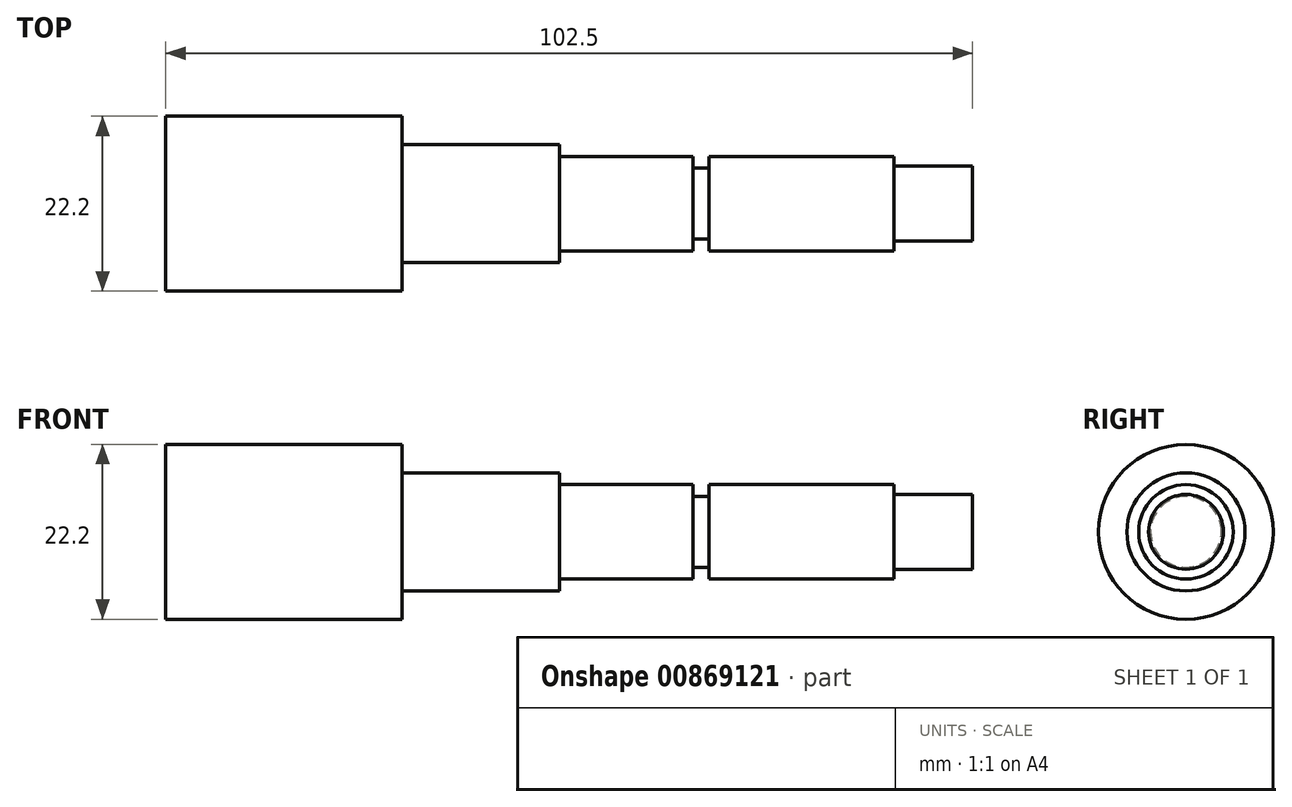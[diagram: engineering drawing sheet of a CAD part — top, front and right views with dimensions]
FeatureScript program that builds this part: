
annotation { "Feature Type Name" : "Feature", "Feature Type Description" : "" }
export const myFeature = defineFeature(function(context is Context, id is Id, definition is map)
    precondition{}
    {
        {
            var Q0;
            Q0=qCreatedBy(makeId("Right.planeOp"),FACE);
            var sketch = newSketch(context, id + "F0", { "sketchPlane" : qUnion([Q0])});
            skCircle(sketch, "E0", {"center": v(0, 0) * mm, "radius": 11.1 * mm});
            skSolve(sketch);
        }
        {
            var Q0;
            Q0 = qSketchRegion(id + "F0", true);
            extrude(context, id + "F1", {"entities" : qUnion([Q0]), "depth" : 30 * mm, "offsetDistance" : 25 * mm});
        }
        {
            var Q0;
            Q0=makeQuery(id+"F1.opExtrude","CAP_FACE",FACE,{"disambiguationData":[OSD([sQuery(id+"F0.wireOp",EDGE,"E0")])],"isStart":false});
            var sketch = newSketch(context, id + "F2", { "sketchPlane" : qUnion([Q0])});
            skCircle(sketch, "E1", {"center": v(0, 0) * mm, "radius": 7.5 * mm});
            skSolve(sketch);
        }
        {
            var Q0;
            Q0 = qSketchRegion(id + "F2", true);
            extrude(context, id + "F3", {"entities" : qUnion([Q0]), "operationType" : NewBodyOperationType.ADD, "depth" : 20 * mm, "offsetDistance" : 25 * mm});
        }
        {
            var Q0;
            Q0=makeQuery(id+"F3.opExtrude","CAP_FACE",FACE,{"disambiguationData":[OSD([sQuery(id+"F2.wireOp",EDGE,"E1")])],"isStart":false});
            var sketch = newSketch(context, id + "F4", { "sketchPlane" : qUnion([Q0])});
            skCircle(sketch, "E2", {"center": v(0, 0) * mm, "radius": 6 * mm});
            skSolve(sketch);
        }
        {
            var Q0;
            Q0 = qSketchRegion(id + "F4", true);
            extrude(context, id + "F5", {"entities" : qUnion([Q0]), "operationType" : NewBodyOperationType.ADD, "depth" : 17 * mm, "offsetDistance" : 25 * mm});
        }
        {
            var Q0;
            Q0=makeQuery(id+"F5.opExtrude","CAP_FACE",FACE,{"disambiguationData":[OSD([sQuery(id+"F4.wireOp",EDGE,"E2")])],"isStart":false});
            var sketch = newSketch(context, id + "F6", { "sketchPlane" : qUnion([Q0])});
            skCircle(sketch, "E3", {"center": v(0, 0) * mm, "radius": 4.5 * mm});
            skSolve(sketch);
        }
        {
            var Q0;
            Q0 = qSketchRegion(id + "F6", true);
            extrude(context, id + "F7", {"entities" : qUnion([Q0]), "operationType" : NewBodyOperationType.ADD, "depth" : (102.5 - 30 - 20 - 17 - 23.5 - 10) * mm, "offsetDistance" : 25 * mm});
        }
        {
            var Q0;
            Q0=makeQuery(id+"F7.opExtrude","CAP_FACE",FACE,{"disambiguationData":[OSD([sQuery(id+"F6.wireOp",EDGE,"E3")])],"isStart":false});
            var sketch = newSketch(context, id + "F8", { "sketchPlane" : qUnion([Q0])});
            skCircle(sketch, "E4", {"center": v(0, 0) * mm, "radius": 6 * mm});
            skSolve(sketch);
        }
        {
            var Q0;
            Q0 = qSketchRegion(id + "F8", true);
            extrude(context, id + "F9", {"entities" : qUnion([Q0]), "operationType" : NewBodyOperationType.ADD, "depth" : 23.5 * mm, "offsetDistance" : 25 * mm});
        }
        {
            var Q0;
            Q0=makeQuery(id+"F9.opExtrude","CAP_FACE",FACE,{"disambiguationData":[OSD([sQuery(id+"F8.wireOp",EDGE,"E4")])],"isStart":false});
            var sketch = newSketch(context, id + "F10", { "sketchPlane" : qUnion([Q0])});
            skCircle(sketch, "E5", {"center": v(0, 0) * mm, "radius": 4.75 * mm});
            skSolve(sketch);
        }
        {
            var Q0;
            Q0 = qSketchRegion(id + "F10", true);
            extrude(context, id + "F11", {"entities" : qUnion([Q0]), "operationType" : NewBodyOperationType.ADD, "depth" : 10 * mm, "offsetDistance" : 25 * mm});
        }
    });
